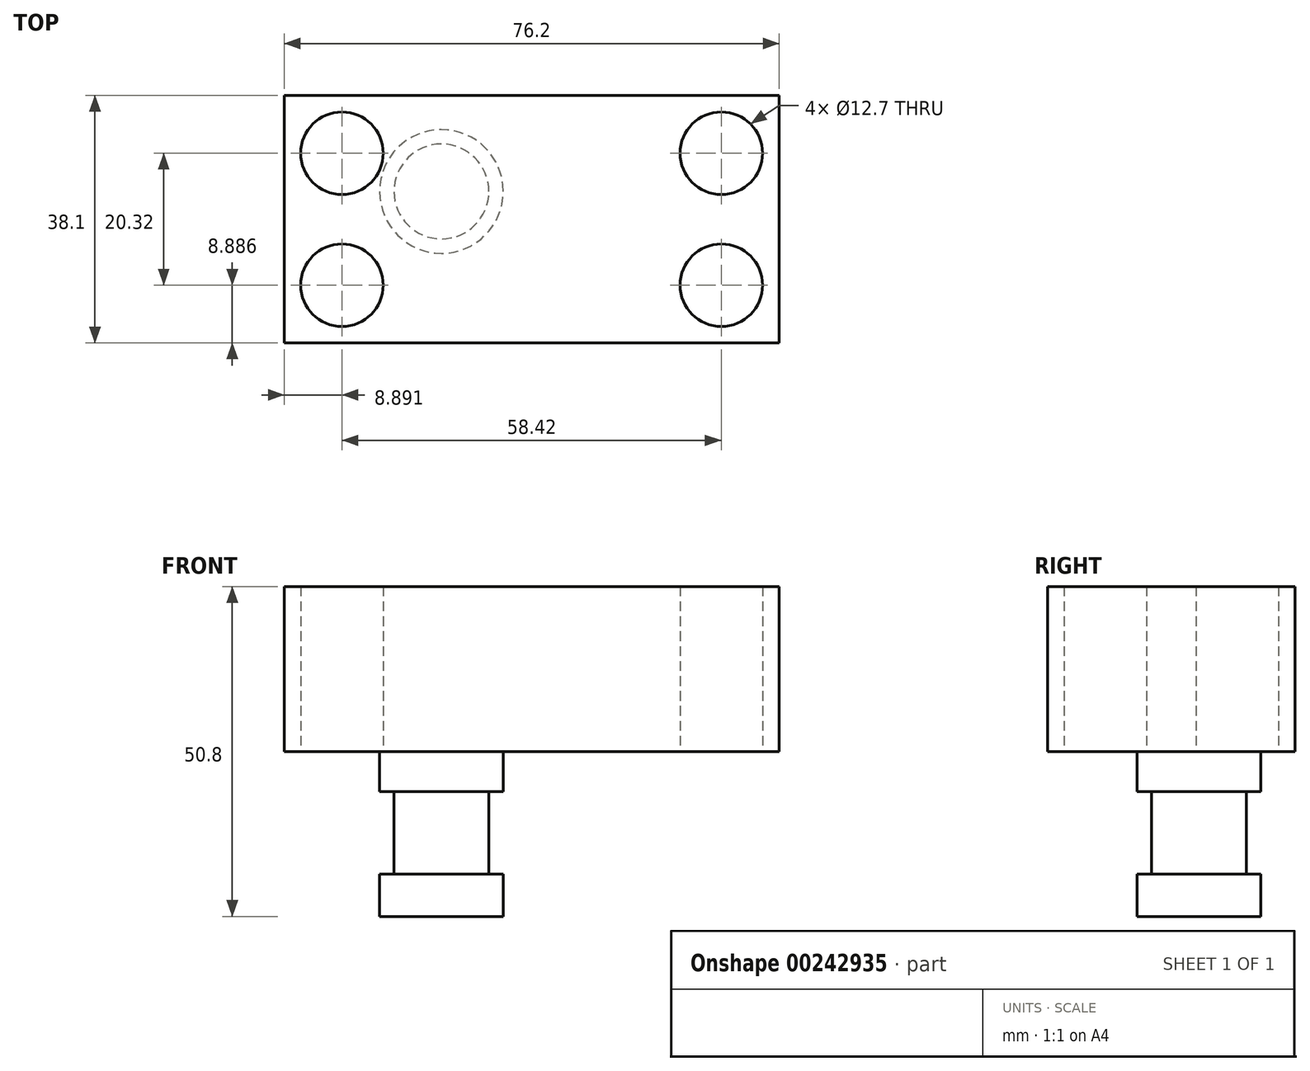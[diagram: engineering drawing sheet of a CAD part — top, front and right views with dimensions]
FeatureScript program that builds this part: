
annotation { "Feature Type Name" : "Feature", "Feature Type Description" : "" }
export const myFeature = defineFeature(function(context is Context, id is Id, definition is map)
    precondition{}
    {
        {
            var Q0;
            Q0=qCreatedBy(makeId("Top.planeOp"),FACE);
            var sketch = newSketch(context, id + "F0", { "sketchPlane" : qUnion([Q0])});
            skLineSegment(sketch, "E0.bottom", {"start": v(-24.2, 14.78) * mm, "end": v(52, 14.78) * mm});
            skLineSegment(sketch, "E0.top", {"start": v(-24.2, -23.32) * mm, "end": v(52, -23.32) * mm});
            skLineSegment(sketch, "E0.left", {"start": v(-24.2, 14.78) * mm, "end": v(-24.2, -23.32) * mm});
            skLineSegment(sketch, "E0.right", {"start": v(52, 14.78) * mm, "end": v(52, -23.32) * mm});
            skSolve(sketch);
        }
        {
            var Q0;
            Q0 = qSketchRegion(id + "F0", true);
            extrude(context, id + "F1", {"entities" : qUnion([Q0]), "depth" : 25.4 * mm});
        }
        {
            var Q0;
            Q0=qCreatedBy(makeId("Top.planeOp"),FACE);
            var sketch = newSketch(context, id + "F2", { "sketchPlane" : qUnion([Q0])});
            skCircle(sketch, "E1", {"center": v(-15.32, 5.89) * mm, "radius": 6.35 * mm});
            skCircle(sketch, "E2", {"center": v(-15.32, -14.43) * mm, "radius": 6.35 * mm});
            skCircle(sketch, "E3", {"center": v(43.1, 5.89) * mm, "radius": 6.35 * mm});
            skCircle(sketch, "E4", {"center": v(43.1, -14.43) * mm, "radius": 6.35 * mm});
            skSolve(sketch);
        }
        {
            var Q0;
            Q0 = qSketchRegion(id + "F2", true);
            extrude(context, id + "F3", {"entities" : qUnion([Q0]), "operationType" : NewBodyOperationType.REMOVE, "depth" : 25.4 * mm});
        }
        {
            var Q0;
            Q0=makeQuery(id+"F1.opExtrude","CAP_FACE",FACE,{"disambiguationData":[OSD([sQuery(id+"F0.wireOp",EDGE,"E0.bottom"),sQuery(id+"F0.wireOp",EDGE,"E0.top"),sQuery(id+"F0.wireOp",EDGE,"E0.left"),sQuery(id+"F0.wireOp",EDGE,"E0.right")])],"isStart":true});
            var sketch = newSketch(context, id + "F4", { "sketchPlane" : qUnion([Q0])});
            skCircle(sketch, "E5", {"center": v(0, 0) * mm, "radius": 9.52 * mm});
            skSolve(sketch);
        }
        {
            var Q0;
            Q0 = qSketchRegion(id + "F4", true);
            extrude(context, id + "F5", {"entities" : qUnion([Q0]), "operationType" : NewBodyOperationType.ADD, "depth" : 25.4 * mm});
        }
        {
            var Q0;
            Q0=qCreatedBy(makeId("Front.planeOp"),FACE);
            var sketch = newSketch(context, id + "F6", { "sketchPlane" : qUnion([Q0])});
            skLineSegment(sketch, "E6.bottom", {"start": v(7.3, -6.22) * mm, "end": v(20, -6.22) * mm});
            skLineSegment(sketch, "E6.top", {"start": v(7.3, -18.92) * mm, "end": v(20, -18.92) * mm});
            skLineSegment(sketch, "E6.left", {"start": v(7.3, -6.22) * mm, "end": v(7.3, -18.92) * mm});
            skLineSegment(sketch, "E6.right", {"start": v(20, -6.22) * mm, "end": v(20, -18.92) * mm});
            skSolve(sketch);
        }
        {
            var Q0;
            Q0 = qSketchRegion(id + "F6", true);
            var Q1;
            Q1=makeQuery(id+"F5.opExtrude","CAP_EDGE",EDGE,{"disambiguationData":[OSD([sQuery(id+"F4.wireOp",EDGE,"E5")])],"isStart":false});
            revolve(context, id + "F7", {"operationType" : NewBodyOperationType.REMOVE, "entities" : qUnion([Q0]), "axis" : qUnion([Q1]), "revolveType" : RevolveType.FULL, "oppositeDirection" : true});
        }
    });
